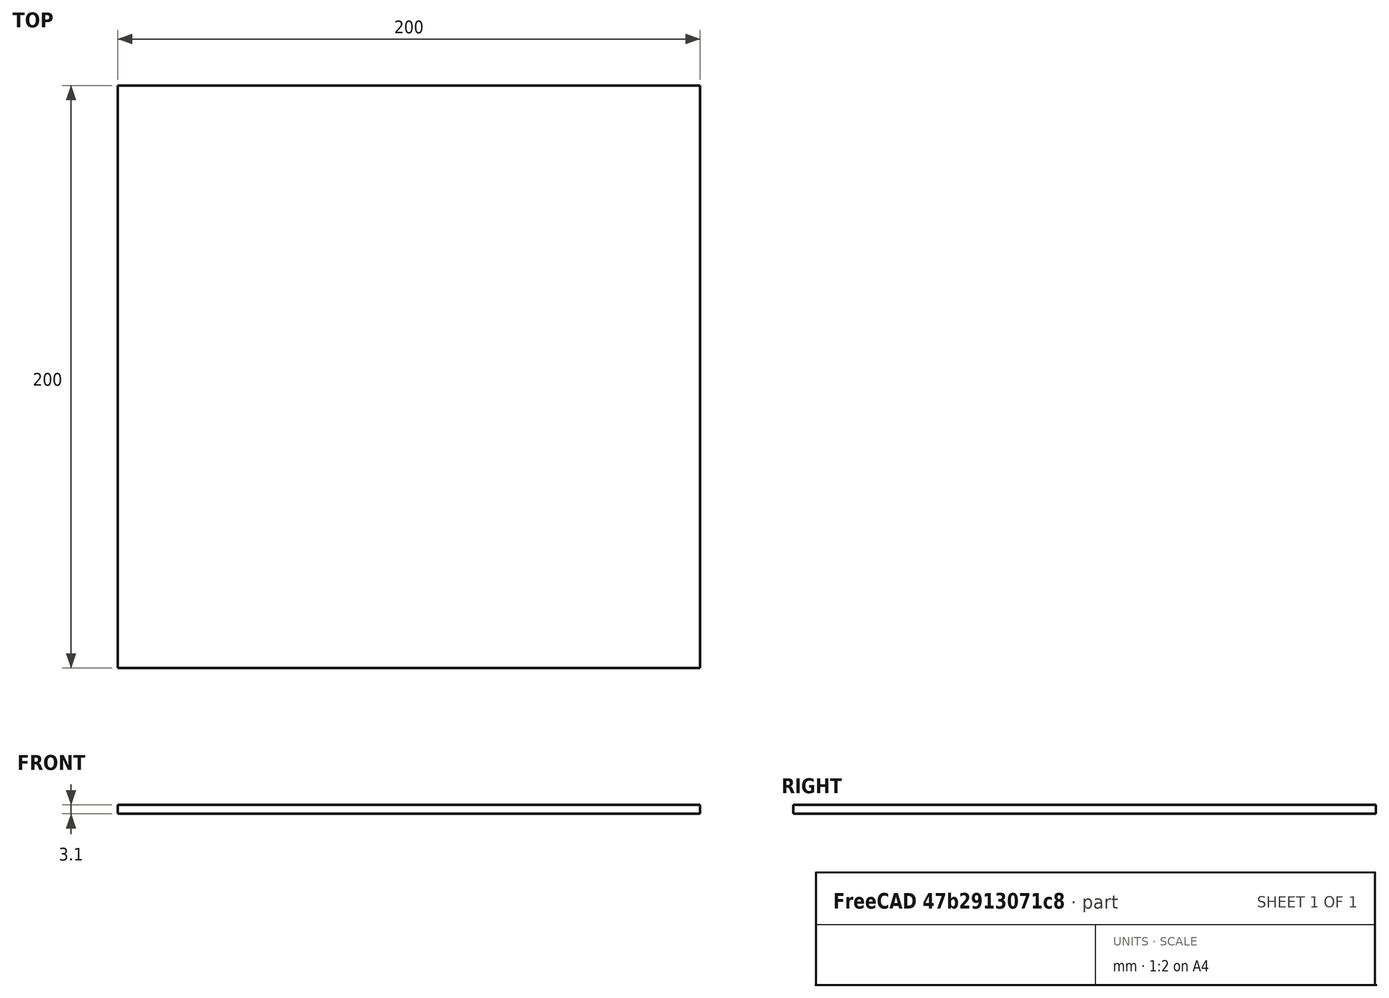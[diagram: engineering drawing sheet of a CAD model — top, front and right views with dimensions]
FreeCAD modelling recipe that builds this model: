
FCSTD DOCUMENT  (FreeCAD 0.19R24276 (Git))
Label: front-plate-test
License: All rights reserved
LicenseURL: http://en.wikipedia.org/wiki/All_rights_reserved
objects: Sketcher::SketchObject×1, PartDesign::Pad×1, PartDesign::Body×1
note: 4 computed .brp shape members not serialized (recipe doc carries the construction recipe); baked Part::Feature solids carry a one-line shape summary decoded from their .brp

FEATURE [Sketcher::SketchObject] Sketch  label="plate"
  FullyConstrained = true
  MapMode = 5
  Support = -> [XY_Plane]
  sketch-geometry (4):
    g0: LineSegment StartX=-100 StartY=100 StartZ=0 EndX=100 EndY=100 EndZ=0
    g1: LineSegment StartX=100 StartY=100 StartZ=0 EndX=100 EndY=-100 EndZ=0
    g2: LineSegment StartX=100 StartY=-100 StartZ=0 EndX=-100 EndY=-100 EndZ=0
    g3: LineSegment StartX=-100 StartY=-100 StartZ=0 EndX=-100 EndY=100 EndZ=0
  constraints (12):
    c: Coincident(g0,g1)
    c: Coincident(g1,g2)
    c: Coincident(g2,g3)
    c: Coincident(g3,g0)
    c: Horizontal(g0)
    c: Horizontal(g2)
    c: Vertical(g1)
    c: Vertical(g3)
    c: DistanceX(g-1,g0) = 100
    c: DistanceX(g0,g-1) = 100
    c: DistanceY(g-1,g0) = 100
    c: DistanceY(g1,g-1) = 100
FEATURE [PartDesign::Pad] Pad  label="plate_pad"
  Direction = (1,1,1)
  Length = 3.1
  Length2 = 100
  Profile = -> Sketch
  Type = 0
FEATURE [PartDesign::Body] Body
  Group = -> [Sketch,Pad]
  Origin = -> Origin
  Tip = -> Pad
